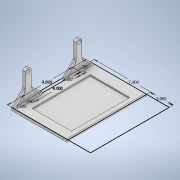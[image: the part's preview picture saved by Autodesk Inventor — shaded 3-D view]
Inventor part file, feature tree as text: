
AUTODESK INVENTOR PART (.ipt)
format: ipt  version: 2020 (Build 240168000, 168)  size: 258,048 bytes
history: native  units: in
note: dims shown in document units (in); Inventor stores cm internally (conversion verified against a paired STEP export)
features: sketch x4, extrude x4, fillet x3, hole x1
ambient origin geometry x8: Origin, YZ Plane, XZ Plane, XY Plane, X Axis, Y Axis, Z Axis, Center Point
bodies: Solid1 (feature_tree)
feature tree (12):
  sketch  "Sketch1"  dims[d0=7.0in d1=7.0in]
  extrude  "Extrusion1"  Depth=7.0in
  extrude  "Extrusion2"  Depth=0.25in
  extrude  "Extrusion3"  Depth=2.2865in
  hole  "Hole1"  [1 undecoded]
  fillet  "Fillet1"  Radius=4.0in
  fillet  "Fillet2"  Radius=2.5in
  fillet  "Fillet3"  Radius=0.25in
  extrude  "Extrusion4"  TaperAngle=45.0deg  [1 undecoded]
  sketch  "Sketch2"  dims[d2=1.0in d3=0.25in]
  sketch  "Sketch3"  dims[d4=5.0in d5=2.2865in]
  sketch  "Sketch4"  dims[d6=4.573in d7=0.5in d8=4.0in d9=2.5in d10=0.0in d11=0.25in d12=0.0in d13=45.0deg d14=0.25in d15=0.0in d18=0.332in d19=0.75in d20=0.635in d21=0.25in d22=0.5635in d23=0.25in d24=0.0in d25=0.1875in d26=0.125in d27=0.125in d28=1.0in d29=1.0in d30=90.0deg d31=3.515in d32=5.18in d33=0.1in d34=0.0in d36=2.25in d37=90.0deg d38=2.25in d39=90.0deg d40=2.0in]
note: 2 required parameter values undecoded (feature->parameter linkage not recoverable at this tier; creation-order binding heuristic only, values carry confidence <= 0.55)
